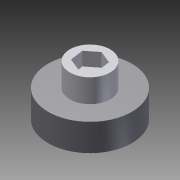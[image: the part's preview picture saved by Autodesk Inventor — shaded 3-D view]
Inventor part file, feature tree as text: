
AUTODESK INVENTOR PART (.ipt)
format: ipt  version: 2012 (Build 160160000, 160)  size: 818,176 bytes
history: native  units: mm
features: other x3, extrude x2, sketch x2, projected_geometry x1
ambient origin geometry x8: Origin, YZ Plane, XZ Plane, XY Plane, X Axis, Y Axis, Z Axis, Center Point
bodies: Solid1 (feature_tree)
feature tree (8):
  other  "MotorToGear.iam"
  other  "Spur Gear2:1"
  other  "MotorToGear.ipt:1"
  extrude  "Extrusion1"  Depth=10.0mm TaperAngle=0.0deg
  extrude  "Extrusion2"  [1 undecoded]
  sketch  "Sketch2"  dims[d0=10.0mm d1=10.0mm d2=0.0mm]
  sketch  "Sketch4"  dims[d3=10.0mm d4=0.0mm]
  projected_geometry  "Projected Loop1"
note: 1 required parameter value undecoded (feature->parameter linkage not recoverable at this tier; creation-order binding heuristic only, values carry confidence <= 0.55)
